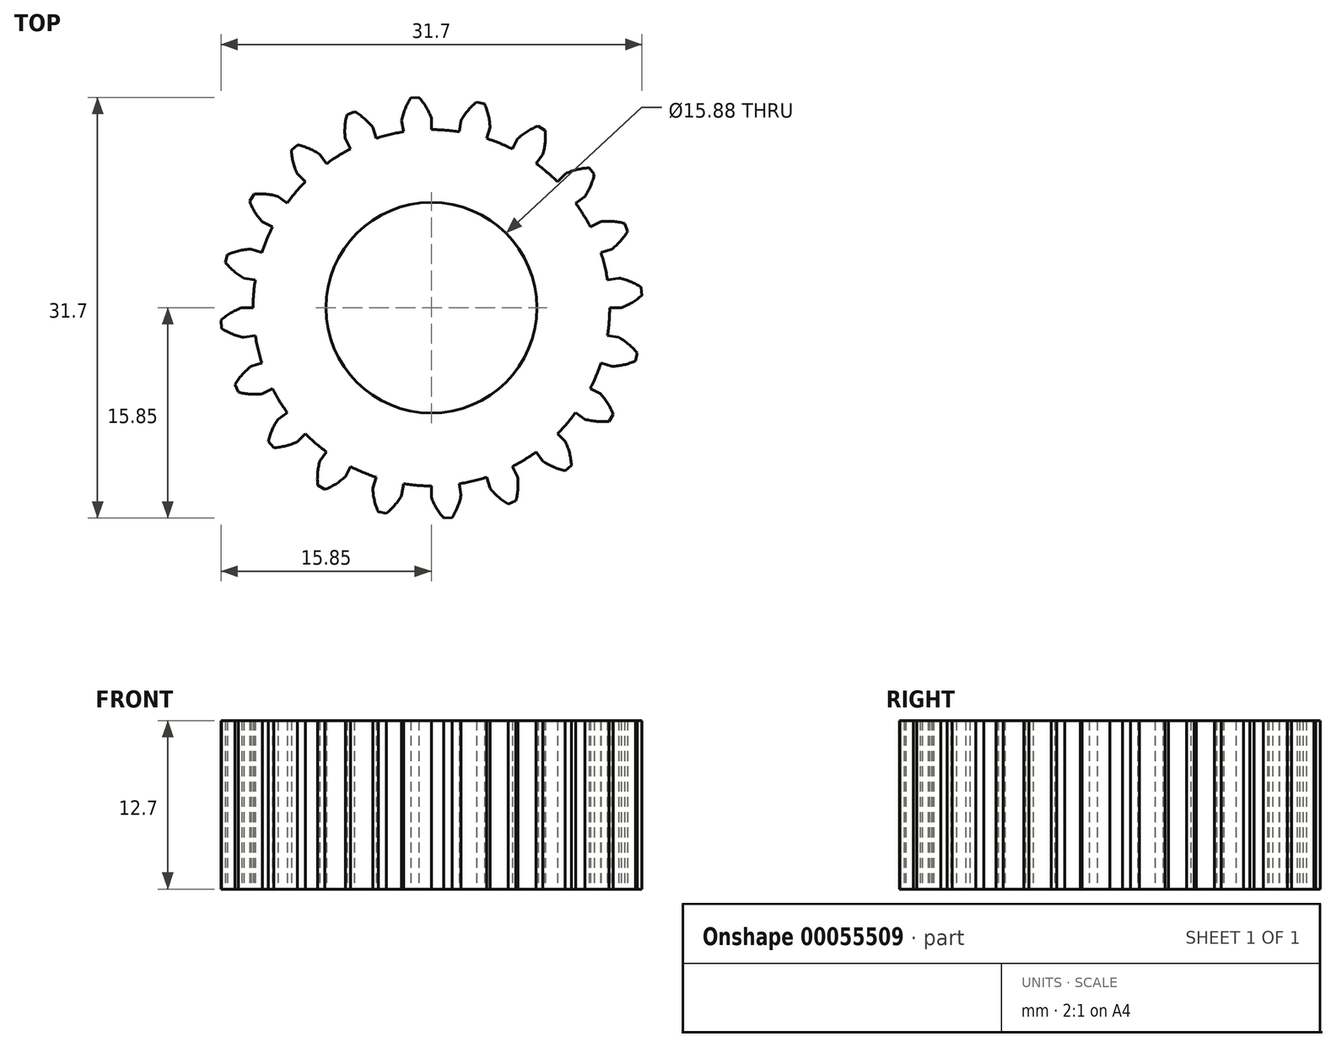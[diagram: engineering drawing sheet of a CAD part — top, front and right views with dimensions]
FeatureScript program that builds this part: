
annotation { "Feature Type Name" : "Feature", "Feature Type Description" : "" }
export const myFeature = defineFeature(function(context is Context, id is Id, definition is map)
    precondition{}
    {
        {
            var Q0;
            Q0=qCreatedBy(makeId("Top.planeOp"),FACE);
            var sketch = newSketch(context, id + "F0", { "sketchPlane" : qUnion([Q0])});
            skCircle(sketch, "E0", {"center": v(0, 0) * mm, "radius": 7.94 * mm});
            skArc(sketch, "E1", {"start": v(-6.1, 11.96) * mm, "mid": v(-7.01, 11.45) * mm, "end": v(-7.9, 10.86) * mm});
            skArc(sketch, "E2.trimOffspring", {"start": v(0, 14.29) * mm, "mid": v(-0.4, 15.11) * mm, "end": v(-0.94, 15.85) * mm});
            skLineSegment(sketch, "E3", {"start": v(0, 14.29) * mm, "end": v(0, 13.43) * mm});
            skLineSegment(sketch, "E4", {"start": v(-0.94, 15.85) * mm, "end": v(-1.25, 15.82) * mm});
            skArc(sketch, "E5.MirrorCS", {"start": v(-2.24, 14.11) * mm, "mid": v(-1.98, 14.99) * mm, "end": v(-1.55, 15.8) * mm});
            skLineSegment(sketch, "E6.MirrorCS", {"start": v(-2.24, 14.11) * mm, "end": v(-2.1, 13.26) * mm});
            skLineSegment(sketch, "E7.MirrorCS", {"start": v(-1.55, 15.8) * mm, "end": v(-1.25, 15.82) * mm});
            skArc(sketch, "E8.1.0", {"start": v(-4.42, 13.59) * mm, "mid": v(-5.04, 14.25) * mm, "end": v(-5.79, 14.78) * mm});
            skArc(sketch, "E8.1.1", {"start": v(-6.49, 12.73) * mm, "mid": v(-6.51, 13.64) * mm, "end": v(-6.36, 14.55) * mm});
            skLineSegment(sketch, "E8.1.2", {"start": v(-6.49, 12.73) * mm, "end": v(-6.1, 11.96) * mm});
            skLineSegment(sketch, "E8.1.3", {"start": v(-4.42, 13.59) * mm, "end": v(-4.15, 12.77) * mm});
            skLineSegment(sketch, "E8.1.4", {"start": v(-6.36, 14.55) * mm, "end": v(-6.07, 14.66) * mm});
            skLineSegment(sketch, "E8.1.5", {"start": v(-5.79, 14.78) * mm, "end": v(-6.07, 14.66) * mm});
            skArc(sketch, "E8.2.0", {"start": v(-8.4, 11.56) * mm, "mid": v(-9.2, 12) * mm, "end": v(-10.07, 12.27) * mm});
            skArc(sketch, "E8.2.1", {"start": v(-10.1, 10.1) * mm, "mid": v(-10.4, 10.96) * mm, "end": v(-10.54, 11.87) * mm});
            skLineSegment(sketch, "E8.2.2", {"start": v(-10.1, 10.1) * mm, "end": v(-9.5, 9.5) * mm});
            skLineSegment(sketch, "E8.2.3", {"start": v(-8.4, 11.56) * mm, "end": v(-7.9, 10.86) * mm});
            skLineSegment(sketch, "E8.2.4", {"start": v(-10.54, 11.87) * mm, "end": v(-10.3, 12.07) * mm});
            skLineSegment(sketch, "E8.2.5", {"start": v(-10.07, 12.27) * mm, "end": v(-10.3, 12.07) * mm});
            skArc(sketch, "E8.3.0", {"start": v(-11.56, 8.4) * mm, "mid": v(-12.46, 8.56) * mm, "end": v(-13.37, 8.56) * mm});
            skArc(sketch, "E8.3.1", {"start": v(-12.73, 6.49) * mm, "mid": v(-13.29, 7.21) * mm, "end": v(-13.7, 8.03) * mm});
            skLineSegment(sketch, "E8.3.2", {"start": v(-12.73, 6.49) * mm, "end": v(-11.96, 6.1) * mm});
            skLineSegment(sketch, "E8.3.3", {"start": v(-11.56, 8.4) * mm, "end": v(-10.86, 7.9) * mm});
            skLineSegment(sketch, "E8.3.4", {"start": v(-13.7, 8.03) * mm, "end": v(-13.53, 8.3) * mm});
            skLineSegment(sketch, "E8.3.5", {"start": v(-13.37, 8.56) * mm, "end": v(-13.53, 8.3) * mm});
            skArc(sketch, "E8.4.0", {"start": v(-13.59, 4.42) * mm, "mid": v(-14.5, 4.3) * mm, "end": v(-15.36, 4) * mm});
            skArc(sketch, "E8.4.1", {"start": v(-14.11, 2.24) * mm, "mid": v(-14.86, 2.75) * mm, "end": v(-15.5, 3.4) * mm});
            skLineSegment(sketch, "E8.4.2", {"start": v(-14.11, 2.24) * mm, "end": v(-13.26, 2.1) * mm});
            skLineSegment(sketch, "E8.4.3", {"start": v(-13.59, 4.42) * mm, "end": v(-12.77, 4.15) * mm});
            skLineSegment(sketch, "E8.4.4", {"start": v(-15.5, 3.4) * mm, "end": v(-15.43, 3.7) * mm});
            skLineSegment(sketch, "E8.4.5", {"start": v(-15.36, 4) * mm, "end": v(-15.43, 3.7) * mm});
            skArc(sketch, "E8.5.0", {"start": v(-14.29, 0) * mm, "mid": v(-15.11, -0.4) * mm, "end": v(-15.85, -0.94) * mm});
            skArc(sketch, "E8.5.1", {"start": v(-14.11, -2.24) * mm, "mid": v(-14.99, -1.98) * mm, "end": v(-15.8, -1.55) * mm});
            skLineSegment(sketch, "E8.5.2", {"start": v(-14.11, -2.24) * mm, "end": v(-13.26, -2.1) * mm});
            skLineSegment(sketch, "E8.5.3", {"start": v(-14.29, 0) * mm, "end": v(-13.43, 0) * mm});
            skLineSegment(sketch, "E8.5.4", {"start": v(-15.8, -1.55) * mm, "end": v(-15.82, -1.25) * mm});
            skLineSegment(sketch, "E8.5.5", {"start": v(-15.85, -0.94) * mm, "end": v(-15.82, -1.25) * mm});
            skArc(sketch, "E8.6.0", {"start": v(-13.59, -4.42) * mm, "mid": v(-14.25, -5.04) * mm, "end": v(-14.78, -5.79) * mm});
            skArc(sketch, "E8.6.1", {"start": v(-12.73, -6.49) * mm, "mid": v(-13.64, -6.51) * mm, "end": v(-14.55, -6.36) * mm});
            skLineSegment(sketch, "E8.6.2", {"start": v(-12.73, -6.49) * mm, "end": v(-11.96, -6.1) * mm});
            skLineSegment(sketch, "E8.6.3", {"start": v(-13.59, -4.42) * mm, "end": v(-12.77, -4.15) * mm});
            skLineSegment(sketch, "E8.6.4", {"start": v(-14.55, -6.36) * mm, "end": v(-14.66, -6.07) * mm});
            skLineSegment(sketch, "E8.6.5", {"start": v(-14.78, -5.79) * mm, "end": v(-14.66, -6.07) * mm});
            skArc(sketch, "E8.7.0", {"start": v(-11.56, -8.4) * mm, "mid": v(-12, -9.2) * mm, "end": v(-12.27, -10.07) * mm});
            skArc(sketch, "E8.7.1", {"start": v(-10.1, -10.1) * mm, "mid": v(-10.96, -10.4) * mm, "end": v(-11.87, -10.54) * mm});
            skLineSegment(sketch, "E8.7.2", {"start": v(-10.1, -10.1) * mm, "end": v(-9.5, -9.5) * mm});
            skLineSegment(sketch, "E8.7.3", {"start": v(-11.56, -8.4) * mm, "end": v(-10.86, -7.9) * mm});
            skLineSegment(sketch, "E8.7.4", {"start": v(-11.87, -10.54) * mm, "end": v(-12.07, -10.3) * mm});
            skLineSegment(sketch, "E8.7.5", {"start": v(-12.27, -10.07) * mm, "end": v(-12.07, -10.3) * mm});
            skArc(sketch, "E8.8.0", {"start": v(-8.4, -11.56) * mm, "mid": v(-8.56, -12.46) * mm, "end": v(-8.56, -13.37) * mm});
            skArc(sketch, "E8.8.1", {"start": v(-6.49, -12.73) * mm, "mid": v(-7.21, -13.29) * mm, "end": v(-8.03, -13.7) * mm});
            skLineSegment(sketch, "E8.8.2", {"start": v(-6.49, -12.73) * mm, "end": v(-6.1, -11.96) * mm});
            skLineSegment(sketch, "E8.8.3", {"start": v(-8.4, -11.56) * mm, "end": v(-7.9, -10.86) * mm});
            skLineSegment(sketch, "E8.8.4", {"start": v(-8.03, -13.7) * mm, "end": v(-8.3, -13.53) * mm});
            skLineSegment(sketch, "E8.8.5", {"start": v(-8.56, -13.37) * mm, "end": v(-8.3, -13.53) * mm});
            skArc(sketch, "E8.9.0", {"start": v(-4.42, -13.59) * mm, "mid": v(-4.3, -14.5) * mm, "end": v(-4, -15.36) * mm});
            skArc(sketch, "E8.9.1", {"start": v(-2.24, -14.11) * mm, "mid": v(-2.75, -14.86) * mm, "end": v(-3.4, -15.5) * mm});
            skLineSegment(sketch, "E8.9.2", {"start": v(-2.24, -14.11) * mm, "end": v(-2.1, -13.26) * mm});
            skLineSegment(sketch, "E8.9.3", {"start": v(-4.42, -13.59) * mm, "end": v(-4.15, -12.77) * mm});
            skLineSegment(sketch, "E8.9.4", {"start": v(-3.4, -15.5) * mm, "end": v(-3.7, -15.43) * mm});
            skLineSegment(sketch, "E8.9.5", {"start": v(-4, -15.36) * mm, "end": v(-3.7, -15.43) * mm});
            skArc(sketch, "E8.10.0", {"start": v(0, -14.29) * mm, "mid": v(0.4, -15.11) * mm, "end": v(0.94, -15.85) * mm});
            skArc(sketch, "E8.10.1", {"start": v(2.24, -14.11) * mm, "mid": v(1.98, -14.99) * mm, "end": v(1.55, -15.8) * mm});
            skLineSegment(sketch, "E8.10.2", {"start": v(2.24, -14.11) * mm, "end": v(2.1, -13.26) * mm});
            skLineSegment(sketch, "E8.10.3", {"start": v(0, -14.29) * mm, "end": v(0, -13.43) * mm});
            skLineSegment(sketch, "E8.10.4", {"start": v(1.55, -15.8) * mm, "end": v(1.25, -15.82) * mm});
            skLineSegment(sketch, "E8.10.5", {"start": v(0.94, -15.85) * mm, "end": v(1.25, -15.82) * mm});
            skArc(sketch, "E8.11.0", {"start": v(4.42, -13.59) * mm, "mid": v(5.04, -14.25) * mm, "end": v(5.79, -14.78) * mm});
            skArc(sketch, "E8.11.1", {"start": v(6.49, -12.73) * mm, "mid": v(6.51, -13.64) * mm, "end": v(6.36, -14.55) * mm});
            skLineSegment(sketch, "E8.11.2", {"start": v(6.49, -12.73) * mm, "end": v(6.1, -11.96) * mm});
            skLineSegment(sketch, "E8.11.3", {"start": v(4.42, -13.59) * mm, "end": v(4.15, -12.77) * mm});
            skLineSegment(sketch, "E8.11.4", {"start": v(6.36, -14.55) * mm, "end": v(6.07, -14.66) * mm});
            skLineSegment(sketch, "E8.11.5", {"start": v(5.79, -14.78) * mm, "end": v(6.07, -14.66) * mm});
            skArc(sketch, "E8.12.0", {"start": v(8.4, -11.56) * mm, "mid": v(9.2, -12) * mm, "end": v(10.07, -12.27) * mm});
            skArc(sketch, "E8.12.1", {"start": v(10.1, -10.1) * mm, "mid": v(10.4, -10.96) * mm, "end": v(10.54, -11.87) * mm});
            skLineSegment(sketch, "E8.12.2", {"start": v(10.1, -10.1) * mm, "end": v(9.5, -9.5) * mm});
            skLineSegment(sketch, "E8.12.3", {"start": v(8.4, -11.56) * mm, "end": v(7.9, -10.86) * mm});
            skLineSegment(sketch, "E8.12.4", {"start": v(10.54, -11.87) * mm, "end": v(10.3, -12.07) * mm});
            skLineSegment(sketch, "E8.12.5", {"start": v(10.07, -12.27) * mm, "end": v(10.3, -12.07) * mm});
            skArc(sketch, "E8.13.0", {"start": v(11.56, -8.4) * mm, "mid": v(12.46, -8.56) * mm, "end": v(13.37, -8.56) * mm});
            skArc(sketch, "E8.13.1", {"start": v(12.73, -6.49) * mm, "mid": v(13.29, -7.21) * mm, "end": v(13.7, -8.03) * mm});
            skLineSegment(sketch, "E8.13.2", {"start": v(12.73, -6.49) * mm, "end": v(11.96, -6.1) * mm});
            skLineSegment(sketch, "E8.13.3", {"start": v(11.56, -8.4) * mm, "end": v(10.86, -7.9) * mm});
            skLineSegment(sketch, "E8.13.4", {"start": v(13.7, -8.03) * mm, "end": v(13.53, -8.3) * mm});
            skLineSegment(sketch, "E8.13.5", {"start": v(13.37, -8.56) * mm, "end": v(13.53, -8.3) * mm});
            skArc(sketch, "E8.14.0", {"start": v(13.59, -4.42) * mm, "mid": v(14.5, -4.3) * mm, "end": v(15.36, -4) * mm});
            skArc(sketch, "E8.14.1", {"start": v(14.11, -2.24) * mm, "mid": v(14.86, -2.75) * mm, "end": v(15.5, -3.4) * mm});
            skLineSegment(sketch, "E8.14.2", {"start": v(14.11, -2.24) * mm, "end": v(13.26, -2.1) * mm});
            skLineSegment(sketch, "E8.14.3", {"start": v(13.59, -4.42) * mm, "end": v(12.77, -4.15) * mm});
            skLineSegment(sketch, "E8.14.4", {"start": v(15.5, -3.4) * mm, "end": v(15.43, -3.7) * mm});
            skLineSegment(sketch, "E8.14.5", {"start": v(15.36, -4) * mm, "end": v(15.43, -3.7) * mm});
            skArc(sketch, "E8.15.0", {"start": v(14.29, 0) * mm, "mid": v(15.11, 0.4) * mm, "end": v(15.85, 0.94) * mm});
            skArc(sketch, "E8.15.1", {"start": v(14.11, 2.24) * mm, "mid": v(14.99, 1.98) * mm, "end": v(15.8, 1.55) * mm});
            skLineSegment(sketch, "E8.15.2", {"start": v(14.11, 2.24) * mm, "end": v(13.26, 2.1) * mm});
            skLineSegment(sketch, "E8.15.3", {"start": v(14.29, 0) * mm, "end": v(13.43, 0) * mm});
            skLineSegment(sketch, "E8.15.4", {"start": v(15.8, 1.55) * mm, "end": v(15.82, 1.25) * mm});
            skLineSegment(sketch, "E8.15.5", {"start": v(15.85, 0.94) * mm, "end": v(15.82, 1.25) * mm});
            skArc(sketch, "E8.16.0", {"start": v(13.59, 4.42) * mm, "mid": v(14.25, 5.04) * mm, "end": v(14.78, 5.79) * mm});
            skArc(sketch, "E8.16.1", {"start": v(12.73, 6.49) * mm, "mid": v(13.64, 6.51) * mm, "end": v(14.55, 6.36) * mm});
            skLineSegment(sketch, "E8.16.2", {"start": v(12.73, 6.49) * mm, "end": v(11.96, 6.1) * mm});
            skLineSegment(sketch, "E8.16.3", {"start": v(13.59, 4.42) * mm, "end": v(12.77, 4.15) * mm});
            skLineSegment(sketch, "E8.16.4", {"start": v(14.55, 6.36) * mm, "end": v(14.66, 6.07) * mm});
            skLineSegment(sketch, "E8.16.5", {"start": v(14.78, 5.79) * mm, "end": v(14.66, 6.07) * mm});
            skArc(sketch, "E8.17.0", {"start": v(11.56, 8.4) * mm, "mid": v(12, 9.2) * mm, "end": v(12.27, 10.07) * mm});
            skArc(sketch, "E8.17.1", {"start": v(10.1, 10.1) * mm, "mid": v(10.96, 10.4) * mm, "end": v(11.87, 10.54) * mm});
            skLineSegment(sketch, "E8.17.2", {"start": v(10.1, 10.1) * mm, "end": v(9.5, 9.5) * mm});
            skLineSegment(sketch, "E8.17.3", {"start": v(11.56, 8.4) * mm, "end": v(10.86, 7.9) * mm});
            skLineSegment(sketch, "E8.17.4", {"start": v(11.87, 10.54) * mm, "end": v(12.07, 10.3) * mm});
            skLineSegment(sketch, "E8.17.5", {"start": v(12.27, 10.07) * mm, "end": v(12.07, 10.3) * mm});
            skArc(sketch, "E8.18.0", {"start": v(8.4, 11.56) * mm, "mid": v(8.56, 12.46) * mm, "end": v(8.56, 13.37) * mm});
            skArc(sketch, "E8.18.1", {"start": v(6.49, 12.73) * mm, "mid": v(7.21, 13.29) * mm, "end": v(8.03, 13.7) * mm});
            skLineSegment(sketch, "E8.18.2", {"start": v(6.49, 12.73) * mm, "end": v(6.1, 11.96) * mm});
            skLineSegment(sketch, "E8.18.3", {"start": v(8.4, 11.56) * mm, "end": v(7.9, 10.86) * mm});
            skLineSegment(sketch, "E8.18.4", {"start": v(8.03, 13.7) * mm, "end": v(8.3, 13.53) * mm});
            skLineSegment(sketch, "E8.18.5", {"start": v(8.56, 13.37) * mm, "end": v(8.3, 13.53) * mm});
            skArc(sketch, "E8.19.0", {"start": v(4.42, 13.59) * mm, "mid": v(4.3, 14.5) * mm, "end": v(4, 15.36) * mm});
            skArc(sketch, "E8.19.1", {"start": v(2.24, 14.11) * mm, "mid": v(2.75, 14.86) * mm, "end": v(3.4, 15.5) * mm});
            skLineSegment(sketch, "E8.19.2", {"start": v(2.24, 14.11) * mm, "end": v(2.1, 13.26) * mm});
            skLineSegment(sketch, "E8.19.3", {"start": v(4.42, 13.59) * mm, "end": v(4.15, 12.77) * mm});
            skLineSegment(sketch, "E8.19.4", {"start": v(3.4, 15.5) * mm, "end": v(3.7, 15.43) * mm});
            skLineSegment(sketch, "E8.19.5", {"start": v(4, 15.36) * mm, "end": v(3.7, 15.43) * mm});
            skArc(sketch, "E9.trimOffspring", {"start": v(-2.1, 13.26) * mm, "mid": v(-3.13, 13.05) * mm, "end": v(-4.15, 12.77) * mm});
            skArc(sketch, "E10.trimOffspring", {"start": v(2.1, 13.26) * mm, "mid": v(1.05, 13.38) * mm, "end": v(0, 13.43) * mm});
            skArc(sketch, "E11.trimOffspring", {"start": v(6.1, 11.96) * mm, "mid": v(5.14, 12.4) * mm, "end": v(4.15, 12.77) * mm});
            skArc(sketch, "E12.trimOffspring", {"start": v(-9.5, 9.5) * mm, "mid": v(-10.2, 8.72) * mm, "end": v(-10.86, 7.9) * mm});
            skArc(sketch, "E13.trimOffspring", {"start": v(-11.96, 6.1) * mm, "mid": v(-12.4, 5.14) * mm, "end": v(-12.77, 4.15) * mm});
            skArc(sketch, "E14.trimOffspring", {"start": v(-13.26, 2.1) * mm, "mid": v(-13.38, 1.05) * mm, "end": v(-13.43, 0) * mm});
            skArc(sketch, "E15.trimOffspring", {"start": v(-13.26, -2.1) * mm, "mid": v(-13.05, -3.13) * mm, "end": v(-12.77, -4.15) * mm});
            skArc(sketch, "E16.trimOffspring", {"start": v(-11.96, -6.1) * mm, "mid": v(-11.45, -7.01) * mm, "end": v(-10.86, -7.9) * mm});
            skArc(sketch, "E17.trimOffspring", {"start": v(-9.5, -9.5) * mm, "mid": v(-8.72, -10.2) * mm, "end": v(-7.9, -10.86) * mm});
            skArc(sketch, "E18.trimOffspring", {"start": v(-6.1, -11.96) * mm, "mid": v(-5.14, -12.4) * mm, "end": v(-4.15, -12.77) * mm});
            skArc(sketch, "E19.trimOffspring", {"start": v(-2.1, -13.26) * mm, "mid": v(-1.05, -13.38) * mm, "end": v(0, -13.43) * mm});
            skArc(sketch, "E20.trimOffspring", {"start": v(2.1, -13.26) * mm, "mid": v(3.13, -13.05) * mm, "end": v(4.15, -12.77) * mm});
            skArc(sketch, "E21.trimOffspring", {"start": v(6.1, -11.96) * mm, "mid": v(7.01, -11.45) * mm, "end": v(7.9, -10.86) * mm});
            skArc(sketch, "E22.trimOffspring", {"start": v(9.5, -9.5) * mm, "mid": v(10.2, -8.72) * mm, "end": v(10.86, -7.9) * mm});
            skArc(sketch, "E23.trimOffspring", {"start": v(11.96, -6.1) * mm, "mid": v(12.4, -5.14) * mm, "end": v(12.77, -4.15) * mm});
            skArc(sketch, "E24.trimOffspring", {"start": v(13.26, -2.1) * mm, "mid": v(13.38, -1.05) * mm, "end": v(13.43, 0) * mm});
            skArc(sketch, "E25.trimOffspring", {"start": v(9.5, 9.5) * mm, "mid": v(8.72, 10.2) * mm, "end": v(7.9, 10.86) * mm});
            skArc(sketch, "E26.trimOffspring", {"start": v(11.96, 6.1) * mm, "mid": v(11.45, 7.01) * mm, "end": v(10.86, 7.9) * mm});
            skArc(sketch, "E27.trimOffspring", {"start": v(13.26, 2.1) * mm, "mid": v(13.05, 3.13) * mm, "end": v(12.77, 4.15) * mm});
            skSolve(sketch);
        }
        {
            var Q0;
            Q0 = qSketchRegion(id + "F0", true);
            extrude(context, id + "F1", {"entities" : qUnion([Q0]), "depth" : 12.7 * mm});
        }
    });
